# Revit family: Chair-Multi_Purpose-Allermuir-ADL10D
name_source: partatom
category: Furniture
revit_build: Autodesk Revit Architecture 2012 (Build: 20110309_2315(x64)
units: mm (PartAtom-declared; Revit-internal decimal feet)

## types (1)
- ADL10D
    04 CSI = 12 51 00
    2.5" Casters = Yes
    95 CSI = 12510
    Advanced Sync Tilt with Multi Position Back = No
    Airflow Back Mesh = No
    Assembly Code = E2020200
    Back = Fabric - Allermuir - Silcoates
    Back Rest = Metal - Allermuir - Chrome - Polished
    Back frame with integral arms in a soft touch Plastic = No
    Base = Metal - Allermuir - Chrome - Polished
    Base or Frame = Polished Chrome center pedestal with adjustable foot ring
    Black Components = Yes
    Black GRP Base = No
    Black Gas Lift = Yes
    Black Plastic Back Membrane = No
    Color Availability = See price list for material options
    Description = 5 Star base fully upholstered, stool
    Glides = Fabric - Allermuir - Silcoates
    Height Adjustable Arms = No
    Height Adjustable Arms with Multi funtction Pad = No
    Height Range = 29.5
    Injection molded sear and back frame in black plastic = No
    Injection molded, contoured back panel in Black Plastic and upholstered seat = No
    Injection molded, contoured seat and back panels in black plastic = No
    Leg Support = Metal - Allermuir - Chrome - Polished
    Manufacturer = Allermuir
    Manufacturer Fax = (419) 887 5805
    Model = ADL10D
    Negative Seat Tilt = No
    Overall Depth = 27"
    Overall Height = 45 1/2"
    Overall Width = 26"
    Pedestal Base = YES
    Plastic Arms in Black = NO
    Plugin Data URL = http://products.ecoscorecard.com
    Polished Aluminum Base = No
    Product Line = Ad-Lib
    Product Page URL = http://www.allermuir.net
    Seat = Fabric - Allermuir - Silcoates
    Seat Depth = 19"
    Seat Depth Adjustment = No
    Seat Height = 29 1/2"
    Seat Height Range = 24"
    Seat Height Range Note = 24"-32"
    Seat Width = 18 179/256"
    Seat or Base = Fabric - Allermuir - Silcoates
    Slimline Upholstery = No
    Stacks = No
    Subcategory = Multi-Purpose Line
    Support = Metal - Allermuir - Chrome - Polished
    Swaged Tubular Steel Legs = NO
    Two Tone Upholstery = Yes
    URL = http://www.allermuir.net
    Upholstered Back = YES
    Upholstered Seat = YES
    Weight = 10.7 lb
    ecoScorecard Product Page = http://products.ecoscorecard.com
    ecoScorecard_data = http://thesenatorgroup.ecoscorecard.com

## geometry (parser evidence)
native form markers: Blend x6, Sweep x1
no freeform markers — native parametric forms only
